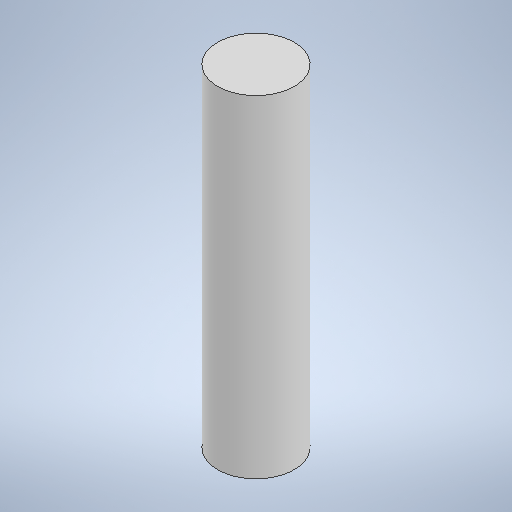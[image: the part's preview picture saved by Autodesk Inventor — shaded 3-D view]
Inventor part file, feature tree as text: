
AUTODESK INVENTOR PART (.ipt)
format: ipt  version: 2025.2 (Build 292293000, 293)  size: 212,480 bytes
history: native  units: mm
features: extrude x1, sketch x1
ambient origin geometry x8: Origin, YZ Plane, XZ Plane, XY Plane, X Axis, Y Axis, Z Axis, Center Point
bodies: Solid1 (feature_tree)
feature tree (2):
  extrude  "Extrusion1"  Depth=13.0mm TaperAngle=0.0deg
  sketch  "Sketch1"  dims[d0=3.0mm d1=13.0mm d2=0.0mm]
